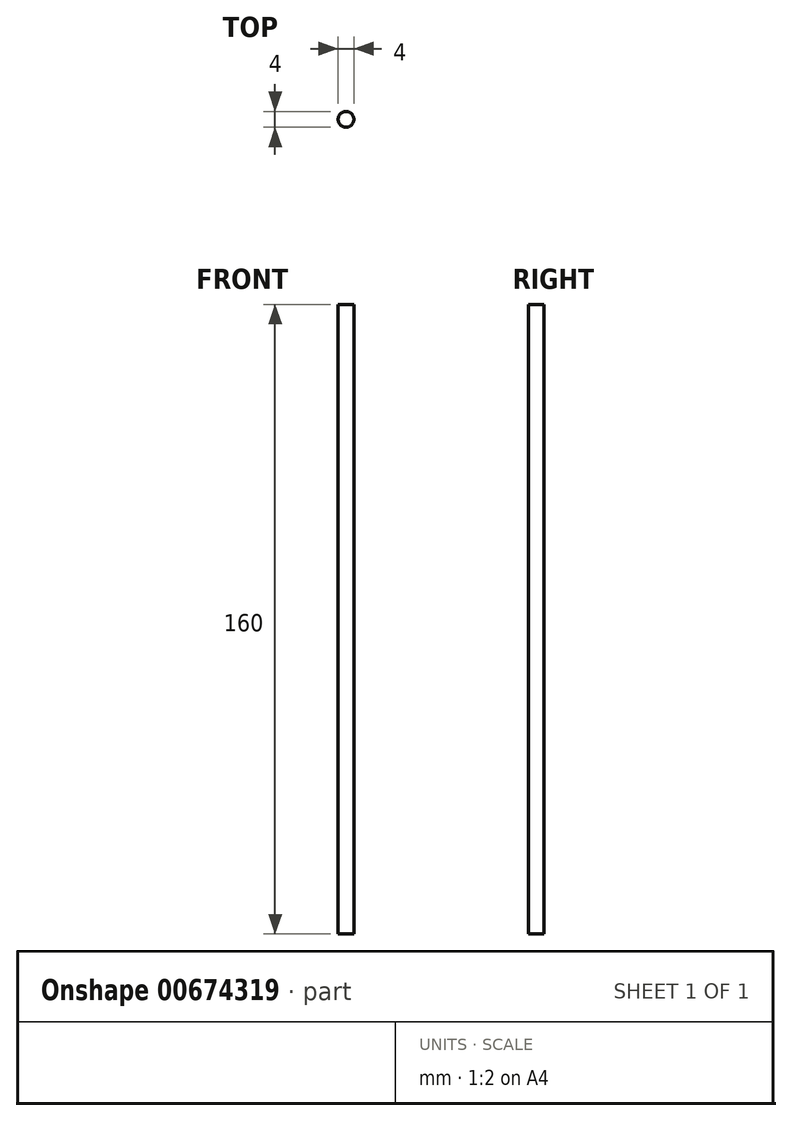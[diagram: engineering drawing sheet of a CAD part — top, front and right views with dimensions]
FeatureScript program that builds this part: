
annotation { "Feature Type Name" : "Feature", "Feature Type Description" : "" }
export const myFeature = defineFeature(function(context is Context, id is Id, definition is map)
    precondition{}
    {
        {
            var Q0;
            Q0=qCreatedBy(makeId("Top.planeOp"),FACE);
            var sketch = newSketch(context, id + "F0", { "sketchPlane" : qUnion([Q0])});
            skCircle(sketch, "E0", {"center": v(0, 0) * mm, "radius": 2 * mm});
            skSolve(sketch);
        }
        {
            var Q0;
            Q0 = qSketchRegion(id + "F0", true);
            extrude(context, id + "F1", {"entities" : qUnion([Q0]), "depth" : 160 * mm, "offsetDistance" : 25 * mm});
        }
    });
